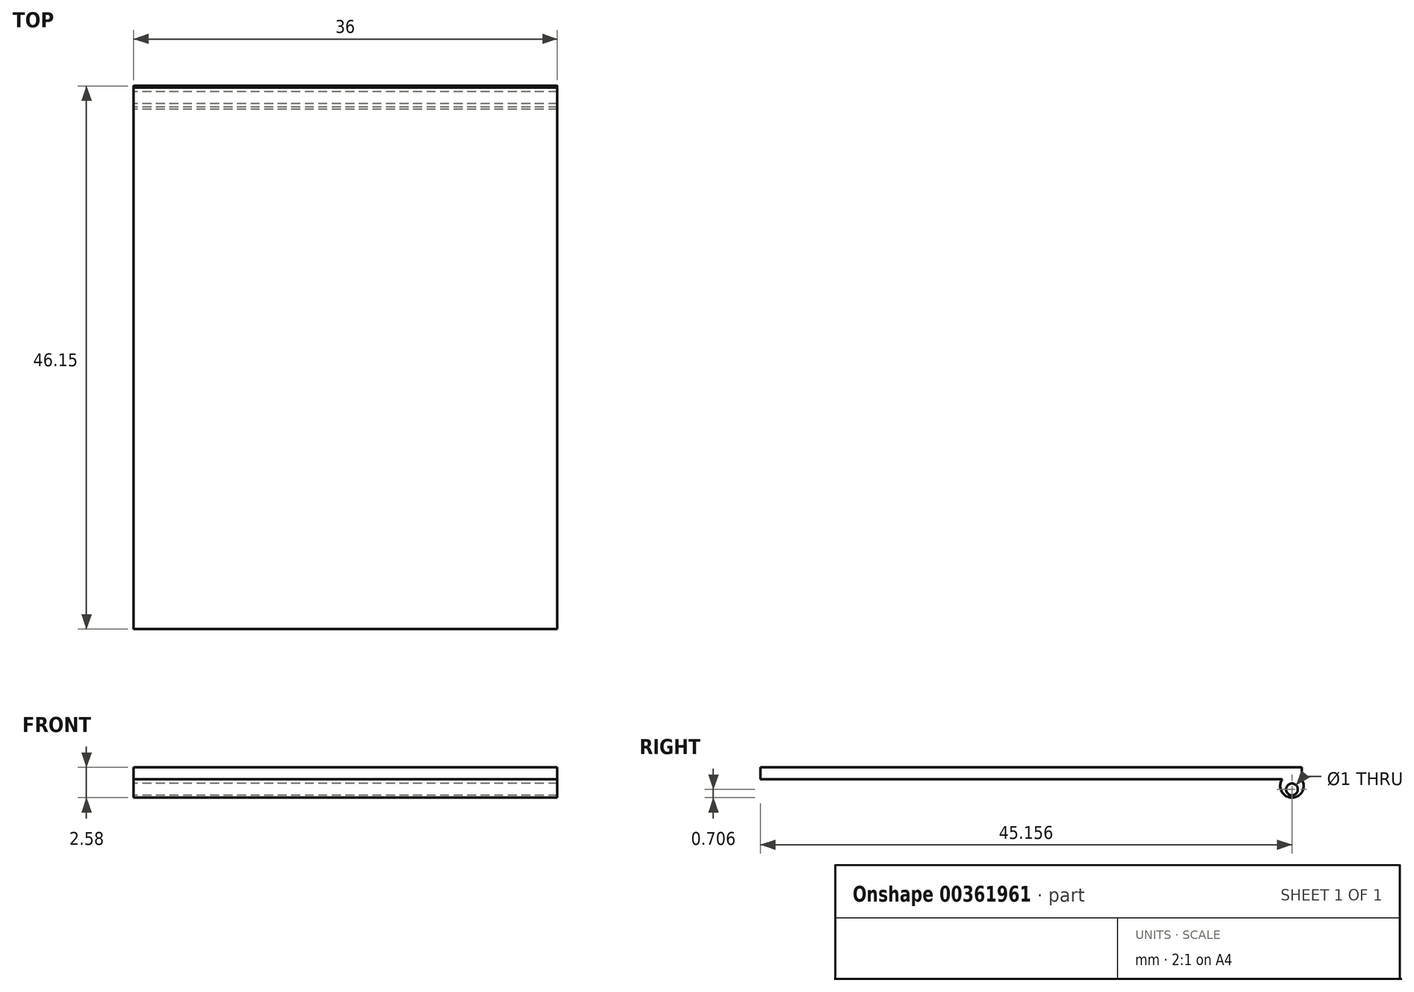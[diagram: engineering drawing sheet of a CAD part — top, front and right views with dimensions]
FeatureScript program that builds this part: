
annotation { "Feature Type Name" : "Feature", "Feature Type Description" : "" }
export const myFeature = defineFeature(function(context is Context, id is Id, definition is map)
    precondition{}
    {
        {
            var Q0;
            Q0=qCreatedBy(makeId("Top.planeOp"),FACE);
            var sketch = newSketch(context, id + "F0", { "sketchPlane" : qUnion([Q0])});
            skLineSegment(sketch, "E0.bottom", {"start": v(18, -23) * mm, "end": v(-18, -23) * mm});
            skLineSegment(sketch, "E0.top", {"start": v(18, 23) * mm, "end": v(-18, 23) * mm});
            skLineSegment(sketch, "E0.left", {"start": v(18, -23) * mm, "end": v(18, 23) * mm});
            skLineSegment(sketch, "E0.right", {"start": v(-18, -23) * mm, "end": v(-18, 23) * mm});
            skPoint(sketch, "E0.middle", {"position": v(0, 0) * mm});
            skSolve(sketch);
        }
        {
            var Q0;
            Q0 = qSketchRegion(id + "F0", true);
            extrude(context, id + "F1", {"entities" : qUnion([Q0]), "depth" : 1 * mm});
        }
        {
            var Q0;
            Q0=qCreatedBy(makeId("Right.planeOp"),FACE);
            var sketch = newSketch(context, id + "F2", { "sketchPlane" : qUnion([Q0])});
            skArc(sketch, "E1", {"start": v(21.35, 0) * mm, "mid": v(22.16, -1.58) * mm, "end": v(22.97, 0) * mm});
            skCircle(sketch, "E2", {"center": v(22.16, -0.87) * mm, "radius": 0.5 * mm});
            skLineSegment(sketch, "E3", {"start": v(22.97, 0) * mm, "end": v(21.35, 0) * mm});
            skSolve(sketch);
        }
        {
            var Q0;
            Q0 = qSketchRegion(id + "F2", true);
            extrude(context, id + "F3", {"entities" : qUnion([Q0]), "operationType" : NewBodyOperationType.ADD, "endBound" : BoundingType.SYMMETRIC, "depth" : 36 * mm});
        }
    });
